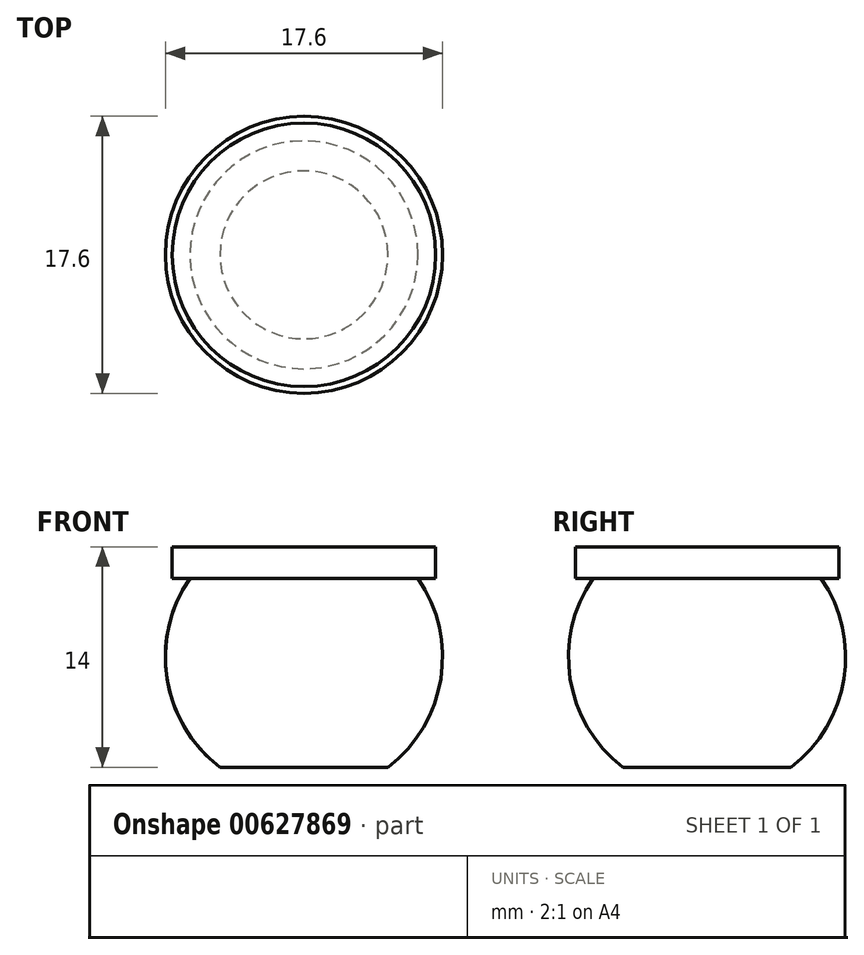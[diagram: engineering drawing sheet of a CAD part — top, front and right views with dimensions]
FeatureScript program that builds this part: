
annotation { "Feature Type Name" : "Feature", "Feature Type Description" : "" }
export const myFeature = defineFeature(function(context is Context, id is Id, definition is map)
    precondition{}
    {
        {
            var Q0;
            Q0=qCreatedBy(makeId("Front.planeOp"),FACE);
            var sketch = newSketch(context, id + "F0", { "sketchPlane" : qUnion([Q0])});
            skLineSegment(sketch, "E0", {"start": v(0, 0) * mm, "end": v(0, 7) * mm});
            skArc(sketch, "E1", {"start": v(5.33, 0) * mm, "mid": v(8.7, 5.62) * mm, "end": v(7.24, 12) * mm});
            skLineSegment(sketch, "E2", {"start": v(0, 7) * mm, "end": v(0, 14) * mm});
            skLineSegment(sketch, "E3", {"start": v(0, 12) * mm, "end": v(7.24, 12) * mm});
            skLineSegment(sketch, "E4", {"start": v(7.24, 12) * mm, "end": v(7.24, 14) * mm});
            skLineSegment(sketch, "E5", {"start": v(5.33, 0) * mm, "end": v(0, 0) * mm});
            skLineSegment(sketch, "E6", {"start": v(7.24, 14) * mm, "end": v(0, 14) * mm});
            skLineSegment(sketch, "E7", {"start": v(7.24, 12) * mm, "end": v(8.37, 12) * mm});
            skLineSegment(sketch, "E8", {"start": v(8.37, 12) * mm, "end": v(8.37, 14) * mm});
            skLineSegment(sketch, "E9", {"start": v(8.37, 14) * mm, "end": v(7.24, 14) * mm});
            skSolve(sketch);
        }
        {
            var Q0;
            {var subQ2=sQuery(id+"F0.wireOp",EDGE,"E0");Q0=makeQuery(id+"F0.imprint","IMPRINT",FACE,{"disambiguationData":[TD([[makeQuery(id+"F0.imprint","IMPRINT",EDGE,{"derivedFrom":subQ2}),-1.0]])]});}
            var Q1;
            Q1=makeQuery(id+"F0.imprint","IMPRINT",FACE,{"disambiguationData":[TD([[makeQuery(id+"F0.imprint","IMPRINT",EDGE,{"derivedFrom":sQuery(id+"F0.wireOp",EDGE,"E4")}),-1.0]])]});
            var Q2;
            {var subQ2=sQuery(id+"F0.wireOp",EDGE,"E3");Q2=makeQuery(id+"F0.imprint","IMPRINT",FACE,{"disambiguationData":[TD([[makeQuery(id+"F0.imprint","IMPRINT",EDGE,{"derivedFrom":subQ2}),1.0]])]});}
            var Q3;
            Q3=sQuery(id+"F0.wireOp",EDGE,"E2");
            revolve(context, id + "F1", {"entities" : qUnion([Q0, Q1, Q2]), "axis" : qUnion([Q3]), "revolveType" : RevolveType.FULL});
        }
    });
